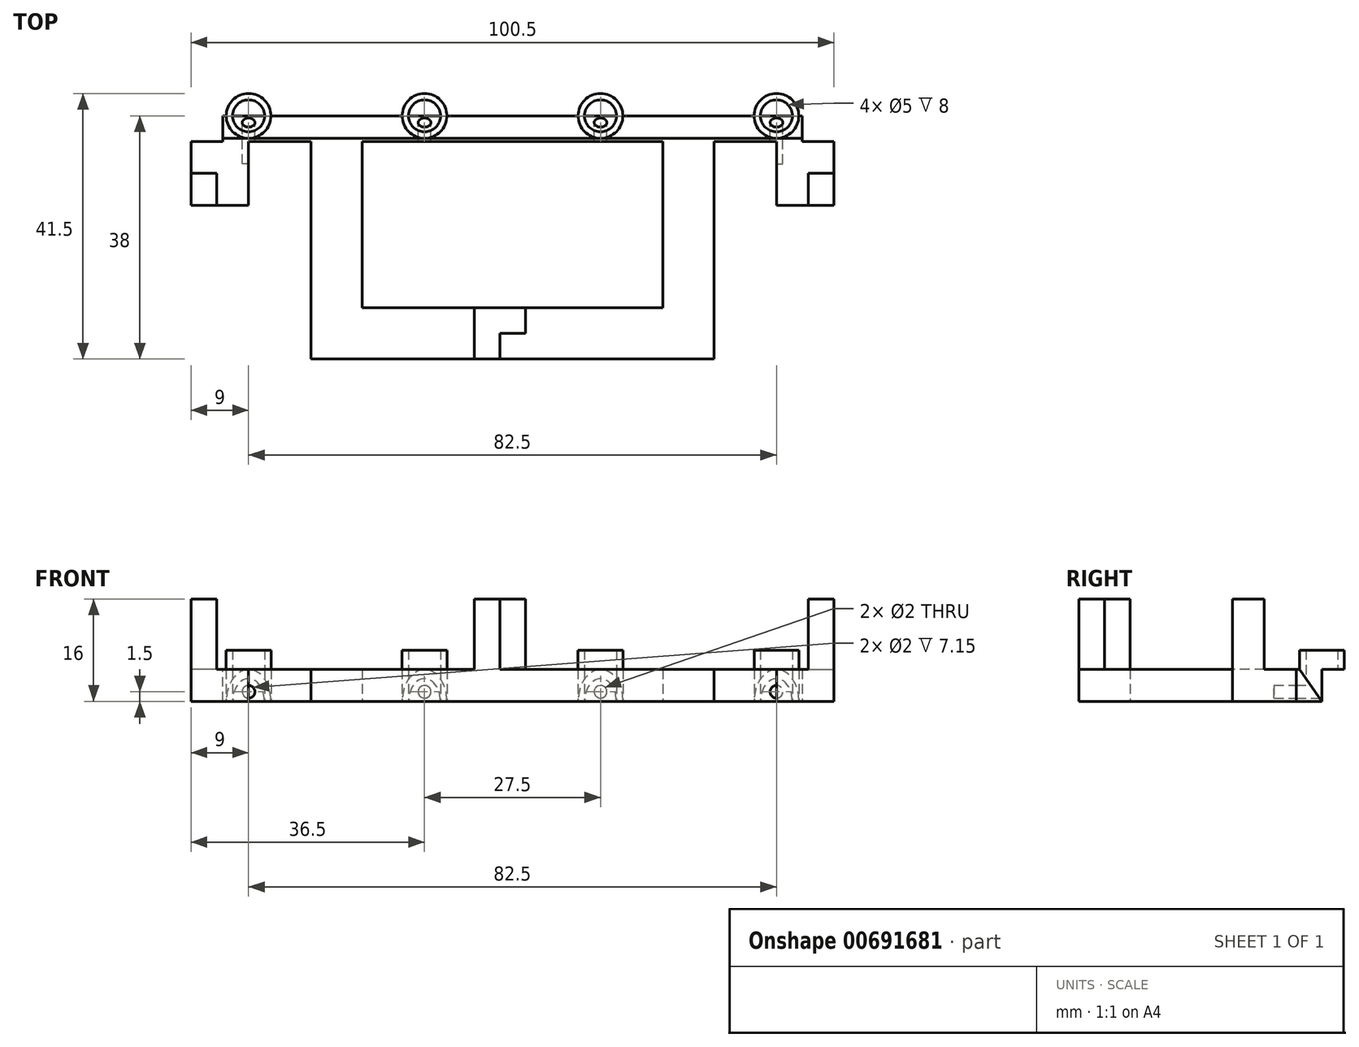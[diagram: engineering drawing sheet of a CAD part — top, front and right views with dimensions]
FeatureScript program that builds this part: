
annotation { "Feature Type Name" : "Feature", "Feature Type Description" : "" }
export const myFeature = defineFeature(function(context is Context, id is Id, definition is map)
    precondition{}
    {
        {
            var Q0;
            Q0=qCreatedBy(makeId("Top.planeOp"),FACE);
            var sketch = newSketch(context, id + "F0", { "sketchPlane" : qUnion([Q0])});
            skLineSegment(sketch, "E0", {"start": v(0, 0) * mm, "end": v(27.5, 0) * mm});
            skLineSegment(sketch, "E1", {"start": v(27.5, 0) * mm, "end": v(55, 0) * mm});
            skLineSegment(sketch, "E2", {"start": v(55, 0) * mm, "end": v(82.5, 0) * mm});
            skCircle(sketch, "E3", {"center": v(0, 0) * mm, "radius": 2.5 * mm});
            skCircle(sketch, "E4", {"center": v(27.5, 0) * mm, "radius": 2.5 * mm});
            skCircle(sketch, "E5", {"center": v(55, 0) * mm, "radius": 2.5 * mm});
            skCircle(sketch, "E6", {"center": v(82.5, 0) * mm, "radius": 2.5 * mm});
            skPoint(sketch, "E7.middle", {"position": v(41.25, 0) * mm});
            skCircle(sketch, "E8", {"center": v(0, 0) * mm, "radius": 4 * mm});
            skCircle(sketch, "E9", {"center": v(27.5, 0) * mm, "radius": 4 * mm});
            skCircle(sketch, "E10", {"center": v(55, 0) * mm, "radius": 4 * mm});
            skCircle(sketch, "E11", {"center": v(82.5, 0) * mm, "radius": 4 * mm});
            skLineSegment(sketch, "E12.bottom", {"start": v(27.5, 4) * mm, "end": v(0, 4) * mm});
            skLineSegment(sketch, "E12.top", {"start": v(27.5, -4) * mm, "end": v(0, -4) * mm});
            skLineSegment(sketch, "E12.left", {"start": v(27.5, 4) * mm, "end": v(27.5, -4) * mm});
            skLineSegment(sketch, "E12.right", {"start": v(0, 4) * mm, "end": v(0, -4) * mm});
            skPoint(sketch, "E12.middle", {"position": v(13.75, 0) * mm});
            skLineSegment(sketch, "E13.bottom", {"start": v(82.5, 4) * mm, "end": v(55, 4) * mm});
            skLineSegment(sketch, "E13.top", {"start": v(82.5, -4) * mm, "end": v(55, -4) * mm});
            skLineSegment(sketch, "E13.left", {"start": v(82.5, 4) * mm, "end": v(82.5, -4) * mm});
            skLineSegment(sketch, "E13.right", {"start": v(55, 4) * mm, "end": v(55, -4) * mm});
            skPoint(sketch, "E13.middle", {"position": v(68.75, 0) * mm});
            skLineSegment(sketch, "E14", {"start": v(13.75, 0) * mm, "end": v(13.75, -30) * mm});
            skLineSegment(sketch, "E15", {"start": v(68.75, 0) * mm, "end": v(68.75, -30) * mm});
            skLineSegment(sketch, "E16.bottom", {"start": v(17.75, 0) * mm, "end": v(9.75, 0) * mm});
            skLineSegment(sketch, "E16.top", {"start": v(17.75, -30) * mm, "end": v(9.75, -30) * mm});
            skLineSegment(sketch, "E16.left", {"start": v(17.75, 0) * mm, "end": v(17.75, -30) * mm});
            skLineSegment(sketch, "E16.right", {"start": v(9.75, 0) * mm, "end": v(9.75, -30) * mm});
            skPoint(sketch, "E16.middle", {"position": v(13.75, -15) * mm});
            skLineSegment(sketch, "E17.bottom", {"start": v(72.75, 0) * mm, "end": v(64.75, 0) * mm});
            skLineSegment(sketch, "E17.top", {"start": v(72.75, -30) * mm, "end": v(64.75, -30) * mm});
            skLineSegment(sketch, "E17.left", {"start": v(72.75, 0) * mm, "end": v(72.75, -30) * mm});
            skLineSegment(sketch, "E17.right", {"start": v(64.75, 0) * mm, "end": v(64.75, -30) * mm});
            skPoint(sketch, "E17.middle", {"position": v(68.75, -15) * mm});
            skLineSegment(sketch, "E18.bottom", {"start": v(9.75, -30) * mm, "end": v(72.75, -30) * mm});
            skLineSegment(sketch, "E18.top", {"start": v(9.75, -38) * mm, "end": v(72.75, -38) * mm});
            skLineSegment(sketch, "E18.left", {"start": v(9.75, -30) * mm, "end": v(9.75, -38) * mm});
            skLineSegment(sketch, "E18.right", {"start": v(72.75, -30) * mm, "end": v(72.75, -38) * mm});
            skLineSegment(sketch, "E19", {"start": v(41.25, -38) * mm, "end": v(41.25, -30) * mm});
            skLineSegment(sketch, "E20", {"start": v(41.25, -38) * mm, "end": v(41.25, -34) * mm});
            skLineSegment(sketch, "E21.bottom", {"start": v(43.25, -38) * mm, "end": v(39.25, -38) * mm});
            skLineSegment(sketch, "E21.top", {"start": v(43.25, -34) * mm, "end": v(39.25, -34) * mm});
            skLineSegment(sketch, "E21.left", {"start": v(43.25, -38) * mm, "end": v(43.25, -34) * mm});
            skLineSegment(sketch, "E21.right", {"start": v(39.25, -38) * mm, "end": v(39.25, -34) * mm});
            skPoint(sketch, "E21.middle", {"position": v(41.25, -36) * mm});
            skLineSegment(sketch, "E22", {"start": v(41.25, -34) * mm, "end": v(41.25, -30) * mm});
            skLineSegment(sketch, "E23.top", {"start": v(43.25, -30) * mm, "end": v(39.25, -30) * mm});
            skLineSegment(sketch, "E23.left", {"start": v(43.25, -34) * mm, "end": v(43.25, -30) * mm});
            skLineSegment(sketch, "E23.right", {"start": v(39.25, -34) * mm, "end": v(39.25, -30) * mm});
            skPoint(sketch, "E23.middle", {"position": v(41.25, -32) * mm});
            skLineSegment(sketch, "E24.bottom", {"start": v(39.25, -38) * mm, "end": v(35.25, -38) * mm});
            skLineSegment(sketch, "E24.top", {"start": v(39.25, -30) * mm, "end": v(35.25, -30) * mm});
            skLineSegment(sketch, "E24.left", {"start": v(39.25, -38) * mm, "end": v(39.25, -30) * mm});
            skLineSegment(sketch, "E24.right", {"start": v(35.25, -38) * mm, "end": v(35.25, -30) * mm});
            skLineSegment(sketch, "E25.bottom", {"start": v(43.25, -38) * mm, "end": v(47.25, -38) * mm});
            skLineSegment(sketch, "E25.top", {"start": v(43.25, -30) * mm, "end": v(47.25, -30) * mm});
            skLineSegment(sketch, "E25.left", {"start": v(43.25, -38) * mm, "end": v(43.25, -30) * mm});
            skLineSegment(sketch, "E25.right", {"start": v(47.25, -38) * mm, "end": v(47.25, -30) * mm});
            skLineSegment(sketch, "E26", {"start": v(0, 0) * mm, "end": v(-4, 0) * mm});
            skLineSegment(sketch, "E27", {"start": v(82.5, 0) * mm, "end": v(86.5, 0) * mm});
            skLineSegment(sketch, "E28.top", {"start": v(0, -4) * mm, "end": v(-4, -4) * mm});
            skLineSegment(sketch, "E28.left", {"start": v(0, 0) * mm, "end": v(0, -4) * mm});
            skLineSegment(sketch, "E28.right", {"start": v(-4, 0) * mm, "end": v(-4, -4) * mm});
            skLineSegment(sketch, "E29.bottom", {"start": v(0, -4) * mm, "end": v(-9, -4) * mm});
            skLineSegment(sketch, "E29.top", {"start": v(0, -14) * mm, "end": v(-9, -14) * mm});
            skLineSegment(sketch, "E29.left", {"start": v(0, -4) * mm, "end": v(0, -14) * mm});
            skLineSegment(sketch, "E29.right", {"start": v(-9, -4) * mm, "end": v(-9, -14) * mm});
            skLineSegment(sketch, "E30.bottom", {"start": v(-9, -14) * mm, "end": v(-5, -14) * mm});
            skLineSegment(sketch, "E30.top", {"start": v(-9, -4) * mm, "end": v(-5, -4) * mm});
            skLineSegment(sketch, "E30.left", {"start": v(-9, -14) * mm, "end": v(-9, -4) * mm});
            skLineSegment(sketch, "E30.right", {"start": v(-5, -14) * mm, "end": v(-5, -4) * mm});
            skLineSegment(sketch, "E31.top", {"start": v(82.5, -4) * mm, "end": v(86.5, -4) * mm});
            skLineSegment(sketch, "E31.left", {"start": v(82.5, 0) * mm, "end": v(82.5, -4) * mm});
            skLineSegment(sketch, "E31.right", {"start": v(86.5, 0) * mm, "end": v(86.5, -4) * mm});
            skLineSegment(sketch, "E32.bottom", {"start": v(82.5, -4) * mm, "end": v(91.5, -4) * mm});
            skLineSegment(sketch, "E32.top", {"start": v(82.5, -14) * mm, "end": v(91.5, -14) * mm});
            skLineSegment(sketch, "E32.left", {"start": v(82.5, -4) * mm, "end": v(82.5, -14) * mm});
            skLineSegment(sketch, "E32.right", {"start": v(91.5, -4) * mm, "end": v(91.5, -14) * mm});
            skLineSegment(sketch, "E33.bottom", {"start": v(91.5, -14) * mm, "end": v(87.5, -14) * mm});
            skLineSegment(sketch, "E33.top", {"start": v(91.5, -4) * mm, "end": v(87.5, -4) * mm});
            skLineSegment(sketch, "E33.left", {"start": v(91.5, -14) * mm, "end": v(91.5, -4) * mm});
            skLineSegment(sketch, "E33.right", {"start": v(87.5, -14) * mm, "end": v(87.5, -4) * mm});
            skLineSegment(sketch, "E34.top", {"start": v(-9, -9) * mm, "end": v(-5, -9) * mm});
            skLineSegment(sketch, "E34.left", {"start": v(-9, -14) * mm, "end": v(-9, -9) * mm});
            skLineSegment(sketch, "E34.right", {"start": v(-5, -14) * mm, "end": v(-5, -9) * mm});
            skLineSegment(sketch, "E35.top", {"start": v(91.5, -9) * mm, "end": v(87.5, -9) * mm});
            skLineSegment(sketch, "E35.left", {"start": v(91.5, -14) * mm, "end": v(91.5, -9) * mm});
            skLineSegment(sketch, "E35.right", {"start": v(87.5, -14) * mm, "end": v(87.5, -9) * mm});
            skLineSegment(sketch, "E36.bottom", {"start": v(27.5, 4) * mm, "end": v(55, 4) * mm});
            skLineSegment(sketch, "E36.top", {"start": v(27.5, -4) * mm, "end": v(55, -4) * mm});
            skSolve(sketch);
        }
        {
            var Q0;
            {var subQ0=sQuery(id+"F0.wireOp",EDGE,"E16.left");var subQ1=sQuery(id+"F0.wireOp",EDGE,"E0");var subQ2=makeQuery(id+"F0.imprint","INTERSECT",VERTEX,{"derivedFrom":[subQ1,subQ0]});Q0=makeQuery(id+"F0.imprint","IMPRINT",FACE,{"disambiguationData":[TD([[makeQuery(id+"F0.imprint","IMPRINT",EDGE,{"disambiguationData":[TD([[subQ2,-1.0]])],"derivedFrom":subQ1}),-1.0]])]});}
            var Q1;
            {var subQ0=sQuery(id+"F0.wireOp",EDGE,"E14");var subQ1=sQuery(id+"F0.wireOp",EDGE,"E12.top");var subQ2=makeQuery(id+"F0.imprint","INTERSECT",VERTEX,{"derivedFrom":[subQ1,subQ0]});Q1=makeQuery(id+"F0.imprint","IMPRINT",FACE,{"disambiguationData":[TD([[makeQuery(id+"F0.imprint","IMPRINT",EDGE,{"disambiguationData":[TD([[subQ2,1.0]])],"derivedFrom":subQ1}),1.0]])]});}
            var Q2;
            {var subQ0=sQuery(id+"F0.wireOp",EDGE,"E10");var subQ1=sQuery(id+"F0.wireOp",EDGE,"E1");var subQ2=makeQuery(id+"F0.imprint","INTERSECT",VERTEX,{"derivedFrom":[subQ1,subQ0]});Q2=makeQuery(id+"F0.imprint","IMPRINT",FACE,{"disambiguationData":[TD([[makeQuery(id+"F0.imprint","IMPRINT",EDGE,{"disambiguationData":[TD([[subQ2,-1.0]])],"derivedFrom":subQ1}),-1.0]])]});}
            var Q3;
            {var subQ3=sQuery(id+"F0.wireOp",EDGE,"E23.left");Q3=makeQuery(id+"F0.imprint","IMPRINT",FACE,{"disambiguationData":[TD([[makeQuery(id+"F0.imprint","IMPRINT",EDGE,{"derivedFrom":subQ3}),1.0]])]});}
            var Q4;
            {var subQ0=sQuery(id+"F0.wireOp",EDGE,"E27");var subQ1=sQuery(id+"F0.wireOp",EDGE,"E6");var subQ2=makeQuery(id+"F0.imprint","INTERSECT",VERTEX,{"derivedFrom":[subQ1,subQ0]});Q4=makeQuery(id+"F0.imprint","IMPRINT",FACE,{"disambiguationData":[TD([[makeQuery(id+"F0.imprint","IMPRINT",EDGE,{"disambiguationData":[TD([[subQ2,1.0]])],"derivedFrom":subQ1}),1.0]])]});}
            var Q5;
            {var subQ1=sQuery(id+"F0.wireOp",EDGE,"E2");var subQ3=sQuery(id+"F0.wireOp",EDGE,"E6");var subQ4=makeQuery(id+"F0.imprint","INTERSECT",VERTEX,{"derivedFrom":[subQ1,subQ3]});Q5=makeQuery(id+"F0.imprint","IMPRINT",FACE,{"disambiguationData":[TD([[makeQuery(id+"F0.imprint","IMPRINT",EDGE,{"disambiguationData":[TD([[subQ4,-1.0]])],"derivedFrom":subQ3}),1.0]])]});}
            var Q6;
            {var subQ1=sQuery(id+"F0.wireOp",EDGE,"E21.left");Q6=makeQuery(id+"F0.imprint","IMPRINT",FACE,{"disambiguationData":[TD([[makeQuery(id+"F0.imprint","IMPRINT",EDGE,{"derivedFrom":subQ1}),-1.0]])]});}
            var Q7;
            {var subQ0=sQuery(id+"F0.wireOp",EDGE,"E10");var subQ1=sQuery(id+"F0.wireOp",EDGE,"E2");var subQ2=makeQuery(id+"F0.imprint","INTERSECT",VERTEX,{"derivedFrom":[subQ1,subQ0]});Q7=makeQuery(id+"F0.imprint","IMPRINT",FACE,{"disambiguationData":[TD([[makeQuery(id+"F0.imprint","IMPRINT",EDGE,{"disambiguationData":[TD([[subQ2,-1.0]])],"derivedFrom":subQ1}),-1.0]])]});}
            var Q8;
            {var subQ0=sQuery(id+"F0.wireOp",EDGE,"E16.right");var subQ1=sQuery(id+"F0.wireOp",EDGE,"E0");var subQ2=makeQuery(id+"F0.imprint","INTERSECT",VERTEX,{"derivedFrom":[subQ1,subQ0]});Q8=makeQuery(id+"F0.imprint","IMPRINT",FACE,{"disambiguationData":[TD([[makeQuery(id+"F0.imprint","IMPRINT",EDGE,{"disambiguationData":[TD([[subQ2,-1.0]])],"derivedFrom":subQ1}),-1.0]])]});}
            var Q9;
            {var subQ3=sQuery(id+"F0.wireOp",EDGE,"E21.left");Q9=makeQuery(id+"F0.imprint","IMPRINT",FACE,{"disambiguationData":[TD([[makeQuery(id+"F0.imprint","IMPRINT",EDGE,{"derivedFrom":subQ3}),1.0]])]});}
            var Q10;
            {var subQ3=sQuery(id+"F0.wireOp",EDGE,"E23.right");Q10=makeQuery(id+"F0.imprint","IMPRINT",FACE,{"disambiguationData":[TD([[makeQuery(id+"F0.imprint","IMPRINT",EDGE,{"derivedFrom":subQ3}),-1.0]])]});}
            var Q11;
            {var subQ0=sQuery(id+"F0.wireOp",EDGE,"E16.right");var subQ1=sQuery(id+"F0.wireOp",EDGE,"E12.top");var subQ2=makeQuery(id+"F0.imprint","INTERSECT",VERTEX,{"derivedFrom":[subQ1,subQ0]});Q11=makeQuery(id+"F0.imprint","IMPRINT",FACE,{"disambiguationData":[TD([[makeQuery(id+"F0.imprint","IMPRINT",EDGE,{"disambiguationData":[TD([[subQ2,1.0]])],"derivedFrom":subQ1}),1.0]])]});}
            var Q12;
            {var subQ0=sQuery(id+"F0.wireOp",EDGE,"E17.left");var subQ1=sQuery(id+"F0.wireOp",EDGE,"E2");var subQ2=makeQuery(id+"F0.imprint","INTERSECT",VERTEX,{"derivedFrom":[subQ1,subQ0]});Q12=makeQuery(id+"F0.imprint","IMPRINT",FACE,{"disambiguationData":[TD([[makeQuery(id+"F0.imprint","IMPRINT",EDGE,{"disambiguationData":[TD([[subQ2,1.0]])],"derivedFrom":subQ1}),-1.0]])]});}
            var Q13;
            {var subQ0=sQuery(id+"F0.wireOp",EDGE,"E9");var subQ1=sQuery(id+"F0.wireOp",EDGE,"E0");var subQ2=makeQuery(id+"F0.imprint","INTERSECT",VERTEX,{"derivedFrom":[subQ1,subQ0]});Q13=makeQuery(id+"F0.imprint","IMPRINT",FACE,{"disambiguationData":[TD([[makeQuery(id+"F0.imprint","IMPRINT",EDGE,{"disambiguationData":[TD([[subQ2,-1.0]])],"derivedFrom":subQ1}),-1.0]])]});}
            var Q14;
            {var subQ3=sQuery(id+"F0.wireOp",EDGE,"E21.right");Q14=makeQuery(id+"F0.imprint","IMPRINT",FACE,{"disambiguationData":[TD([[makeQuery(id+"F0.imprint","IMPRINT",EDGE,{"derivedFrom":subQ3}),-1.0]])]});}
            var Q15;
            {var subQ1=sQuery(id+"F0.wireOp",EDGE,"E21.right");Q15=makeQuery(id+"F0.imprint","IMPRINT",FACE,{"disambiguationData":[TD([[makeQuery(id+"F0.imprint","IMPRINT",EDGE,{"derivedFrom":subQ1}),1.0]])]});}
            var Q16;
            {var subQ0=sQuery(id+"F0.wireOp",EDGE,"E10");var subQ1=sQuery(id+"F0.wireOp",EDGE,"E2");var subQ2=makeQuery(id+"F0.imprint","INTERSECT",VERTEX,{"derivedFrom":[subQ1,subQ0]});Q16=makeQuery(id+"F0.imprint","IMPRINT",FACE,{"disambiguationData":[TD([[makeQuery(id+"F0.imprint","IMPRINT",EDGE,{"disambiguationData":[TD([[subQ2,1.0]])],"derivedFrom":subQ1}),-1.0]])]});}
            var Q17;
            {var subQ0=sQuery(id+"F0.wireOp",EDGE,"E15");var subQ1=sQuery(id+"F0.wireOp",EDGE,"E13.top");var subQ2=makeQuery(id+"F0.imprint","INTERSECT",VERTEX,{"derivedFrom":[subQ1,subQ0]});Q17=makeQuery(id+"F0.imprint","IMPRINT",FACE,{"disambiguationData":[TD([[makeQuery(id+"F0.imprint","IMPRINT",EDGE,{"disambiguationData":[TD([[subQ2,1.0]])],"derivedFrom":subQ1}),1.0]])]});}
            var Q18;
            {var subQ0=sQuery(id+"F0.wireOp",EDGE,"E17.right");var subQ1=sQuery(id+"F0.wireOp",EDGE,"E2");var subQ2=makeQuery(id+"F0.imprint","INTERSECT",VERTEX,{"derivedFrom":[subQ1,subQ0]});Q18=makeQuery(id+"F0.imprint","IMPRINT",FACE,{"disambiguationData":[TD([[makeQuery(id+"F0.imprint","IMPRINT",EDGE,{"disambiguationData":[TD([[subQ2,-1.0]])],"derivedFrom":subQ1}),-1.0]])]});}
            var Q19;
            {var subQ1=sQuery(id+"F0.wireOp",EDGE,"E1");var subQ3=sQuery(id+"F0.wireOp",EDGE,"E5");var subQ4=makeQuery(id+"F0.imprint","INTERSECT",VERTEX,{"derivedFrom":[subQ1,subQ3]});Q19=makeQuery(id+"F0.imprint","IMPRINT",FACE,{"disambiguationData":[TD([[makeQuery(id+"F0.imprint","IMPRINT",EDGE,{"disambiguationData":[TD([[subQ4,-1.0]])],"derivedFrom":subQ3}),1.0]])]});}
            var Q20;
            {var subQ0=sQuery(id+"F0.wireOp",EDGE,"E26");var subQ1=sQuery(id+"F0.wireOp",EDGE,"E3");var subQ2=makeQuery(id+"F0.imprint","INTERSECT",VERTEX,{"derivedFrom":[subQ1,subQ0]});Q20=makeQuery(id+"F0.imprint","IMPRINT",FACE,{"disambiguationData":[TD([[makeQuery(id+"F0.imprint","IMPRINT",EDGE,{"disambiguationData":[TD([[subQ2,-1.0]])],"derivedFrom":subQ1}),-1.0]])]});}
            var Q21;
            {var subQ5=sQuery(id+"F0.wireOp",EDGE,"E31.top");Q21=makeQuery(id+"F0.imprint","IMPRINT",FACE,{"disambiguationData":[TD([[makeQuery(id+"F0.imprint","IMPRINT",EDGE,{"derivedFrom":subQ5}),-1.0]])]});}
            var Q22;
            {var subQ2=sQuery(id+"F0.wireOp",EDGE,"E28.top");Q22=makeQuery(id+"F0.imprint","IMPRINT",FACE,{"disambiguationData":[TD([[makeQuery(id+"F0.imprint","IMPRINT",EDGE,{"derivedFrom":subQ2}),-1.0]])]});}
            var Q23;
            {var subQ0=sQuery(id+"F0.wireOp",EDGE,"E31.top");Q23=makeQuery(id+"F0.imprint","IMPRINT",FACE,{"disambiguationData":[TD([[makeQuery(id+"F0.imprint","IMPRINT",EDGE,{"derivedFrom":subQ0}),1.0]])]});}
            var Q24;
            {var subQ5=sQuery(id+"F0.wireOp",EDGE,"E34.top");Q24=makeQuery(id+"F0.imprint","IMPRINT",FACE,{"disambiguationData":[TD([[makeQuery(id+"F0.imprint","IMPRINT",EDGE,{"derivedFrom":subQ5}),1.0]])]});}
            var Q25;
            {var subQ5=sQuery(id+"F0.wireOp",EDGE,"E35.top");Q25=makeQuery(id+"F0.imprint","IMPRINT",FACE,{"disambiguationData":[TD([[makeQuery(id+"F0.imprint","IMPRINT",EDGE,{"derivedFrom":subQ5}),-1.0]])]});}
            var Q26;
            {var subQ5=sQuery(id+"F0.wireOp",EDGE,"E34.top");Q26=makeQuery(id+"F0.imprint","IMPRINT",FACE,{"disambiguationData":[TD([[makeQuery(id+"F0.imprint","IMPRINT",EDGE,{"derivedFrom":subQ5}),-1.0]])]});}
            var Q27;
            {var subQ5=sQuery(id+"F0.wireOp",EDGE,"E35.top");Q27=makeQuery(id+"F0.imprint","IMPRINT",FACE,{"disambiguationData":[TD([[makeQuery(id+"F0.imprint","IMPRINT",EDGE,{"derivedFrom":subQ5}),1.0]])]});}
            var Q28;
            {var subQ1=sQuery(id+"F0.wireOp",EDGE,"E0");var subQ3=sQuery(id+"F0.wireOp",EDGE,"E3");var subQ4=makeQuery(id+"F0.imprint","INTERSECT",VERTEX,{"derivedFrom":[subQ1,subQ3]});Q28=makeQuery(id+"F0.imprint","IMPRINT",FACE,{"disambiguationData":[TD([[makeQuery(id+"F0.imprint","IMPRINT",EDGE,{"disambiguationData":[TD([[subQ4,1.0]])],"derivedFrom":subQ3}),1.0]])]});}
            var Q29;
            {var subQ0=sQuery(id+"F0.wireOp",EDGE,"E8");var subQ1=sQuery(id+"F0.wireOp",EDGE,"E0");var subQ2=makeQuery(id+"F0.imprint","INTERSECT",VERTEX,{"derivedFrom":[subQ1,subQ0]});Q29=makeQuery(id+"F0.imprint","IMPRINT",FACE,{"disambiguationData":[TD([[makeQuery(id+"F0.imprint","IMPRINT",EDGE,{"disambiguationData":[TD([[subQ2,-1.0]])],"derivedFrom":subQ1}),-1.0]])]});}
            var Q30;
            {var subQ0=sQuery(id+"F0.wireOp",EDGE,"E4");var subQ1=sQuery(id+"F0.wireOp",EDGE,"E0");var subQ2=makeQuery(id+"F0.imprint","INTERSECT",VERTEX,{"derivedFrom":[subQ1,subQ0]});Q30=makeQuery(id+"F0.imprint","IMPRINT",FACE,{"disambiguationData":[TD([[makeQuery(id+"F0.imprint","IMPRINT",EDGE,{"disambiguationData":[TD([[subQ2,-1.0]])],"derivedFrom":subQ0}),1.0]])]});}
            var Q31;
            {var subQ1=sQuery(id+"F0.wireOp",EDGE,"E1");var subQ3=sQuery(id+"F0.wireOp",EDGE,"E4");var subQ4=makeQuery(id+"F0.imprint","INTERSECT",VERTEX,{"derivedFrom":[subQ1,subQ3]});Q31=makeQuery(id+"F0.imprint","IMPRINT",FACE,{"disambiguationData":[TD([[makeQuery(id+"F0.imprint","IMPRINT",EDGE,{"disambiguationData":[TD([[subQ4,1.0]])],"derivedFrom":subQ3}),1.0]])]});}
            var Q32;
            {var subQ0=sQuery(id+"F0.wireOp",EDGE,"E15");var subQ1=sQuery(id+"F0.wireOp",EDGE,"E13.top");var subQ2=makeQuery(id+"F0.imprint","INTERSECT",VERTEX,{"derivedFrom":[subQ1,subQ0]});Q32=makeQuery(id+"F0.imprint","IMPRINT",FACE,{"disambiguationData":[TD([[makeQuery(id+"F0.imprint","IMPRINT",EDGE,{"disambiguationData":[TD([[subQ2,-1.0]])],"derivedFrom":subQ1}),1.0]])]});}
            var Q33;
            {var subQ0=sQuery(id+"F0.wireOp",EDGE,"E9");var subQ1=sQuery(id+"F0.wireOp",EDGE,"E1");var subQ2=makeQuery(id+"F0.imprint","INTERSECT",VERTEX,{"derivedFrom":[subQ1,subQ0]});Q33=makeQuery(id+"F0.imprint","IMPRINT",FACE,{"disambiguationData":[TD([[makeQuery(id+"F0.imprint","IMPRINT",EDGE,{"disambiguationData":[TD([[subQ2,1.0]])],"derivedFrom":subQ1}),-1.0]])]});}
            var Q34;
            {var subQ0=sQuery(id+"F0.wireOp",EDGE,"E26");var subQ1=sQuery(id+"F0.wireOp",EDGE,"E3");var subQ2=makeQuery(id+"F0.imprint","INTERSECT",VERTEX,{"derivedFrom":[subQ1,subQ0]});Q34=makeQuery(id+"F0.imprint","IMPRINT",FACE,{"disambiguationData":[TD([[makeQuery(id+"F0.imprint","IMPRINT",EDGE,{"disambiguationData":[TD([[subQ2,-1.0]])],"derivedFrom":subQ1}),1.0]])]});}
            var Q35;
            {var subQ1=sQuery(id+"F0.wireOp",EDGE,"E2");var subQ3=sQuery(id+"F0.wireOp",EDGE,"E5");var subQ4=makeQuery(id+"F0.imprint","INTERSECT",VERTEX,{"derivedFrom":[subQ1,subQ3]});Q35=makeQuery(id+"F0.imprint","IMPRINT",FACE,{"disambiguationData":[TD([[makeQuery(id+"F0.imprint","IMPRINT",EDGE,{"disambiguationData":[TD([[subQ4,1.0]])],"derivedFrom":subQ3}),1.0]])]});}
            var Q36;
            {var subQ0=sQuery(id+"F0.wireOp",EDGE,"E27");var subQ1=sQuery(id+"F0.wireOp",EDGE,"E6");var subQ2=makeQuery(id+"F0.imprint","INTERSECT",VERTEX,{"derivedFrom":[subQ1,subQ0]});Q36=makeQuery(id+"F0.imprint","IMPRINT",FACE,{"disambiguationData":[TD([[makeQuery(id+"F0.imprint","IMPRINT",EDGE,{"disambiguationData":[TD([[subQ2,1.0]])],"derivedFrom":subQ1}),-1.0]])]});}
            var Q37;
            {var subQ0=sQuery(id+"F0.wireOp",EDGE,"E18.left");Q37=makeQuery(id+"F0.imprint","IMPRINT",FACE,{"disambiguationData":[TD([[makeQuery(id+"F0.imprint","IMPRINT",EDGE,{"derivedFrom":subQ0}),1.0]])]});}
            var Q38;
            {var subQ5=sQuery(id+"F0.wireOp",EDGE,"E36.top");Q38=makeQuery(id+"F0.imprint","IMPRINT",FACE,{"disambiguationData":[TD([[makeQuery(id+"F0.imprint","IMPRINT",EDGE,{"derivedFrom":subQ5}),1.0]])]});}
            var Q39;
            {var subQ0=sQuery(id+"F0.wireOp",EDGE,"E17.left");var subQ1=sQuery(id+"F0.wireOp",EDGE,"E2");var subQ2=makeQuery(id+"F0.imprint","INTERSECT",VERTEX,{"derivedFrom":[subQ1,subQ0]});Q39=makeQuery(id+"F0.imprint","IMPRINT",FACE,{"disambiguationData":[TD([[makeQuery(id+"F0.imprint","IMPRINT",EDGE,{"disambiguationData":[TD([[subQ2,-1.0]])],"derivedFrom":subQ1}),-1.0]])]});}
            var Q40;
            {var subQ0=sQuery(id+"F0.wireOp",EDGE,"E16.left");var subQ1=sQuery(id+"F0.wireOp",EDGE,"E0");var subQ2=makeQuery(id+"F0.imprint","INTERSECT",VERTEX,{"derivedFrom":[subQ1,subQ0]});Q40=makeQuery(id+"F0.imprint","IMPRINT",FACE,{"disambiguationData":[TD([[makeQuery(id+"F0.imprint","IMPRINT",EDGE,{"disambiguationData":[TD([[subQ2,1.0]])],"derivedFrom":subQ1}),-1.0]])]});}
            var Q41;
            {var subQ0=sQuery(id+"F0.wireOp",EDGE,"E8");var subQ1=sQuery(id+"F0.wireOp",EDGE,"E0");var subQ2=makeQuery(id+"F0.imprint","INTERSECT",VERTEX,{"derivedFrom":[subQ1,subQ0]});Q41=makeQuery(id+"F0.imprint","IMPRINT",FACE,{"disambiguationData":[TD([[makeQuery(id+"F0.imprint","IMPRINT",EDGE,{"disambiguationData":[TD([[subQ2,1.0]])],"derivedFrom":subQ1}),-1.0]])]});}
            var Q42;
            {var subQ0=sQuery(id+"F0.wireOp",EDGE,"E18.right");Q42=makeQuery(id+"F0.imprint","IMPRINT",FACE,{"disambiguationData":[TD([[makeQuery(id+"F0.imprint","IMPRINT",EDGE,{"derivedFrom":subQ0}),-1.0]])]});}
            var Q43;
            {var subQ5=sQuery(id+"F0.wireOp",EDGE,"E28.top");Q43=makeQuery(id+"F0.imprint","IMPRINT",FACE,{"disambiguationData":[TD([[makeQuery(id+"F0.imprint","IMPRINT",EDGE,{"derivedFrom":subQ5}),1.0]])]});}
            var Q44;
            {var subQ0=sQuery(id+"F0.wireOp",EDGE,"E11");var subQ1=sQuery(id+"F0.wireOp",EDGE,"E2");var subQ2=makeQuery(id+"F0.imprint","INTERSECT",VERTEX,{"derivedFrom":[subQ1,subQ0]});Q44=makeQuery(id+"F0.imprint","IMPRINT",FACE,{"disambiguationData":[TD([[makeQuery(id+"F0.imprint","IMPRINT",EDGE,{"disambiguationData":[TD([[subQ2,-1.0]])],"derivedFrom":subQ1}),-1.0]])]});}
            extrude(context, id + "F1", {"entities" : qUnion([Q0, Q1, Q2, Q3, Q4, Q5, Q6, Q7, Q8, Q9, Q10, Q11, Q12, Q13, Q14, Q15, Q16, Q17, Q18, Q19, Q20, Q21, Q22, Q23, Q24, Q25, Q26, Q27, Q28, Q29, Q30, Q31, Q32, Q33, Q34, Q35, Q36, Q37, Q38, Q39, Q40, Q41, Q42, Q43, Q44]), "depth" : 5 * mm, "offsetDistance" : 25 * mm});
        }
        {
            var Q0;
            {var subQ5=sQuery(id+"F0.wireOp",EDGE,"E34.top");Q0=makeQuery(id+"F0.imprint","IMPRINT",FACE,{"disambiguationData":[TD([[makeQuery(id+"F0.imprint","IMPRINT",EDGE,{"derivedFrom":subQ5}),-1.0]])]});}
            var Q1;
            {var subQ5=sQuery(id+"F0.wireOp",EDGE,"E35.top");Q1=makeQuery(id+"F0.imprint","IMPRINT",FACE,{"disambiguationData":[TD([[makeQuery(id+"F0.imprint","IMPRINT",EDGE,{"derivedFrom":subQ5}),1.0]])]});}
            var Q2;
            {var subQ1=sQuery(id+"F0.wireOp",EDGE,"E21.right");Q2=makeQuery(id+"F0.imprint","IMPRINT",FACE,{"disambiguationData":[TD([[makeQuery(id+"F0.imprint","IMPRINT",EDGE,{"derivedFrom":subQ1}),1.0]])]});}
            var Q3;
            {var subQ3=sQuery(id+"F0.wireOp",EDGE,"E23.right");Q3=makeQuery(id+"F0.imprint","IMPRINT",FACE,{"disambiguationData":[TD([[makeQuery(id+"F0.imprint","IMPRINT",EDGE,{"derivedFrom":subQ3}),-1.0]])]});}
            var Q4;
            {var subQ3=sQuery(id+"F0.wireOp",EDGE,"E23.left");Q4=makeQuery(id+"F0.imprint","IMPRINT",FACE,{"disambiguationData":[TD([[makeQuery(id+"F0.imprint","IMPRINT",EDGE,{"derivedFrom":subQ3}),1.0]])]});}
            extrude(context, id + "F2", {"entities" : qUnion([Q0, Q1, Q2, Q3, Q4]), "operationType" : NewBodyOperationType.ADD, "depth" : 16 * mm, "offsetDistance" : 25 * mm});
        }
        {
            var Q0;
            Q0=makeQuery(id+"F1.opExtrude","CAP_FACE",FACE,{"disambiguationData":[OSD([sQuery(id+"F0.wireOp",EDGE,"E0"),sQuery(id+"F0.wireOp",EDGE,"E1"),sQuery(id+"F0.wireOp",EDGE,"E2"),sQuery(id+"F0.wireOp",EDGE,"E12.top"),sQuery(id+"F0.wireOp",EDGE,"E13.top"),sQuery(id+"F0.wireOp",EDGE,"E16.left"),sQuery(id+"F0.wireOp",EDGE,"E16.right"),sQuery(id+"F0.wireOp",EDGE,"E17.left"),sQuery(id+"F0.wireOp",EDGE,"E17.right"),sQuery(id+"F0.wireOp",EDGE,"E18.bottom"),sQuery(id+"F0.wireOp",EDGE,"E18.top"),sQuery(id+"F0.wireOp",EDGE,"E18.left"),sQuery(id+"F0.wireOp",EDGE,"E18.right"),sQuery(id+"F0.wireOp",EDGE,"E26"),sQuery(id+"F0.wireOp",EDGE,"E27"),sQuery(id+"F0.wireOp",EDGE,"E28.right"),sQuery(id+"F0.wireOp",EDGE,"E29.bottom"),sQuery(id+"F0.wireOp",EDGE,"E29.top"),sQuery(id+"F0.wireOp",EDGE,"E29.left"),sQuery(id+"F0.wireOp",EDGE,"E29.right"),sQuery(id+"F0.wireOp",EDGE,"E31.right"),sQuery(id+"F0.wireOp",EDGE,"E32.bottom"),sQuery(id+"F0.wireOp",EDGE,"E32.top"),sQuery(id+"F0.wireOp",EDGE,"E32.left"),sQuery(id+"F0.wireOp",EDGE,"E32.right"),sQuery(id+"F0.wireOp",EDGE,"E36.top")])],"isStart":false});
            var sketch = newSketch(context, id + "F3", { "sketchPlane" : qUnion([Q0])});
            skCircle(sketch, "E37", {"center": v(0, 0) * mm, "radius": 2.5 * mm});
            skCircle(sketch, "E38", {"center": v(0, 0) * mm, "radius": 3.5 * mm});
            skLineSegment(sketch, "E39", {"start": v(0, 0) * mm, "end": v(27.5, 0) * mm});
            skLineSegment(sketch, "E40", {"start": v(27.5, 0) * mm, "end": v(55, 0) * mm});
            skLineSegment(sketch, "E41", {"start": v(55, 0) * mm, "end": v(82.5, 0) * mm});
            skCircle(sketch, "E42", {"center": v(27.5, 0) * mm, "radius": 3.5 * mm});
            skCircle(sketch, "E43", {"center": v(55, 0) * mm, "radius": 3.5 * mm});
            skCircle(sketch, "E44", {"center": v(82.5, 0) * mm, "radius": 3.5 * mm});
            skCircle(sketch, "E45", {"center": v(27.5, 0) * mm, "radius": 2.5 * mm});
            skCircle(sketch, "E46", {"center": v(55, 0) * mm, "radius": 2.5 * mm});
            skCircle(sketch, "E47", {"center": v(82.5, 0) * mm, "radius": 2.5 * mm});
            skSolve(sketch);
        }
        {
            var Q0;
            Q0 = qSketchRegion(id + "F3", true);
            extrude(context, id + "F4", {"entities" : qUnion([Q0]), "operationType" : NewBodyOperationType.ADD, "depth" : 3 * mm, "offsetDistance" : 25 * mm});
        }
        {
            var Q0;
            Q0=makeQuery(id+"F1.opExtrude","SWEPT_FACE",FACE,{"disambiguationData":[OSD([sQuery(id+"F0.wireOp",EDGE,"E0"),sQuery(id+"F0.wireOp",EDGE,"E1"),sQuery(id+"F0.wireOp",EDGE,"E2"),sQuery(id+"F0.wireOp",EDGE,"E26"),sQuery(id+"F0.wireOp",EDGE,"E27")])]});
            var sketch = newSketch(context, id + "F5", { "sketchPlane" : qUnion([Q0])});
            skLineSegment(sketch, "E48", {"start": v(0, 0) * mm, "end": v(0, 3) * mm});
            skCircle(sketch, "E49", {"center": v(0, 1.5) * mm, "radius": 1 * mm});
            skLineSegment(sketch, "E50", {"start": v(0, 0) * mm, "end": v(-27.5, 0) * mm});
            skLineSegment(sketch, "E51", {"start": v(-27.5, 0) * mm, "end": v(-55, 0) * mm});
            skLineSegment(sketch, "E52", {"start": v(-55, 0) * mm, "end": v(-82.5, 0) * mm});
            skLineSegment(sketch, "E53", {"start": v(-82.5, 0) * mm, "end": v(-82.5, 3) * mm});
            skLineSegment(sketch, "E54", {"start": v(-55, 0) * mm, "end": v(-55, 3) * mm});
            skLineSegment(sketch, "E55", {"start": v(-27.5, 0) * mm, "end": v(-27.5, 3) * mm});
            skCircle(sketch, "E56", {"center": v(-27.5, 1.5) * mm, "radius": 1 * mm});
            skCircle(sketch, "E57", {"center": v(-55, 1.5) * mm, "radius": 1 * mm});
            skCircle(sketch, "E58", {"center": v(-82.5, 1.5) * mm, "radius": 1 * mm});
            skSolve(sketch);
        }
        {
            var Q0;
            Q0 = qSketchRegion(id + "F5", true);
            extrude(context, id + "F6", {"entities" : qUnion([Q0]), "operationType" : NewBodyOperationType.REMOVE, "oppositeDirection" : true, "depth" : 7.5 * mm, "offsetDistance" : 25 * mm});
        }
        {
            var Q0;
            {var subQ0=sQuery(id+"F0.wireOp",EDGE,"E27");var subQ1=sQuery(id+"F0.wireOp",EDGE,"E26");var subQ2=sQuery(id+"F0.wireOp",EDGE,"E2");var subQ3=sQuery(id+"F0.wireOp",EDGE,"E1");var subQ4=sQuery(id+"F0.wireOp",EDGE,"E0");Q0=makeQuery(id+"F4.boolean.opBoolean","SPLIT",EDGE,{"disambiguationData":[topologyDisambiguationEdgeConnected([makeQuery(id+"F1.opExtrude","SWEPT_FACE",FACE,{"disambiguationData":[OSD([subQ4,subQ3,subQ2,subQ1,subQ0])]}),makeQuery(id+"F4.opExtrude","CAP_FACE",FACE,{"disambiguationData":[OSD([sQuery(id+"F3.wireOp",EDGE,"E37"),sQuery(id+"F3.wireOp",EDGE,"E38")])],"isStart":true})]),OD(0.0)],"derivedFrom":makeQuery(id+"F1.opExtrude","CAP_EDGE",EDGE,{"disambiguationData":[OSD([subQ4,subQ3,subQ2,subQ1,subQ0])],"isStart":false})});}
            var Q1;
            {var subQ0=sQuery(id+"F0.wireOp",EDGE,"E27");var subQ1=sQuery(id+"F0.wireOp",EDGE,"E26");var subQ2=sQuery(id+"F0.wireOp",EDGE,"E2");var subQ3=sQuery(id+"F0.wireOp",EDGE,"E1");var subQ4=sQuery(id+"F0.wireOp",EDGE,"E0");Q1=makeQuery(id+"F4.boolean.opBoolean","SPLIT",EDGE,{"disambiguationData":[topologyDisambiguationEdgeConnected([makeQuery(id+"F1.opExtrude","SWEPT_FACE",FACE,{"disambiguationData":[OSD([subQ4,subQ3,subQ2,subQ1,subQ0])]}),makeQuery(id+"F4.opExtrude","CAP_FACE",FACE,{"disambiguationData":[OSD([sQuery(id+"F3.wireOp",EDGE,"E42"),sQuery(id+"F3.wireOp",EDGE,"E45")])],"isStart":true})]),OD(0.0)],"derivedFrom":makeQuery(id+"F1.opExtrude","CAP_EDGE",EDGE,{"disambiguationData":[OSD([subQ4,subQ3,subQ2,subQ1,subQ0])],"isStart":false})});}
            var Q2;
            {var subQ0=sQuery(id+"F0.wireOp",EDGE,"E27");var subQ1=sQuery(id+"F0.wireOp",EDGE,"E26");var subQ2=sQuery(id+"F0.wireOp",EDGE,"E2");var subQ3=sQuery(id+"F0.wireOp",EDGE,"E1");var subQ4=sQuery(id+"F0.wireOp",EDGE,"E0");Q2=makeQuery(id+"F4.boolean.opBoolean","SPLIT",EDGE,{"disambiguationData":[topologyDisambiguationEdgeConnected([makeQuery(id+"F1.opExtrude","SWEPT_FACE",FACE,{"disambiguationData":[OSD([subQ4,subQ3,subQ2,subQ1,subQ0])]}),makeQuery(id+"F4.opExtrude","CAP_FACE",FACE,{"disambiguationData":[OSD([sQuery(id+"F3.wireOp",EDGE,"E43"),sQuery(id+"F3.wireOp",EDGE,"E46")])],"isStart":true})]),OD(1.0)],"derivedFrom":makeQuery(id+"F1.opExtrude","CAP_EDGE",EDGE,{"disambiguationData":[OSD([subQ4,subQ3,subQ2,subQ1,subQ0])],"isStart":false})});}
            var Q3;
            {var subQ0=sQuery(id+"F0.wireOp",EDGE,"E27");var subQ1=sQuery(id+"F0.wireOp",EDGE,"E26");var subQ2=sQuery(id+"F0.wireOp",EDGE,"E2");var subQ3=sQuery(id+"F0.wireOp",EDGE,"E1");var subQ4=sQuery(id+"F0.wireOp",EDGE,"E0");Q3=makeQuery(id+"F4.boolean.opBoolean","SPLIT",EDGE,{"disambiguationData":[topologyDisambiguationEdgeConnected([makeQuery(id+"F1.opExtrude","SWEPT_FACE",FACE,{"disambiguationData":[OSD([subQ4,subQ3,subQ2,subQ1,subQ0])]}),makeQuery(id+"F4.opExtrude","CAP_FACE",FACE,{"disambiguationData":[OSD([sQuery(id+"F3.wireOp",EDGE,"E44"),sQuery(id+"F3.wireOp",EDGE,"E47")])],"isStart":true})]),OD(1.0)],"derivedFrom":makeQuery(id+"F1.opExtrude","CAP_EDGE",EDGE,{"disambiguationData":[OSD([subQ4,subQ3,subQ2,subQ1,subQ0])],"isStart":false})});}
            chamfer(context, id + "F7", {"entities" : qUnion([Q0, Q1, Q2, Q3]), "chamferType" : ChamferType.TWO_OFFSETS, "width1" : 5 * mm, "oppositeDirection" : false, "width2" : 3.5 * mm, "tangentPropagation" : true});
        }
    });
